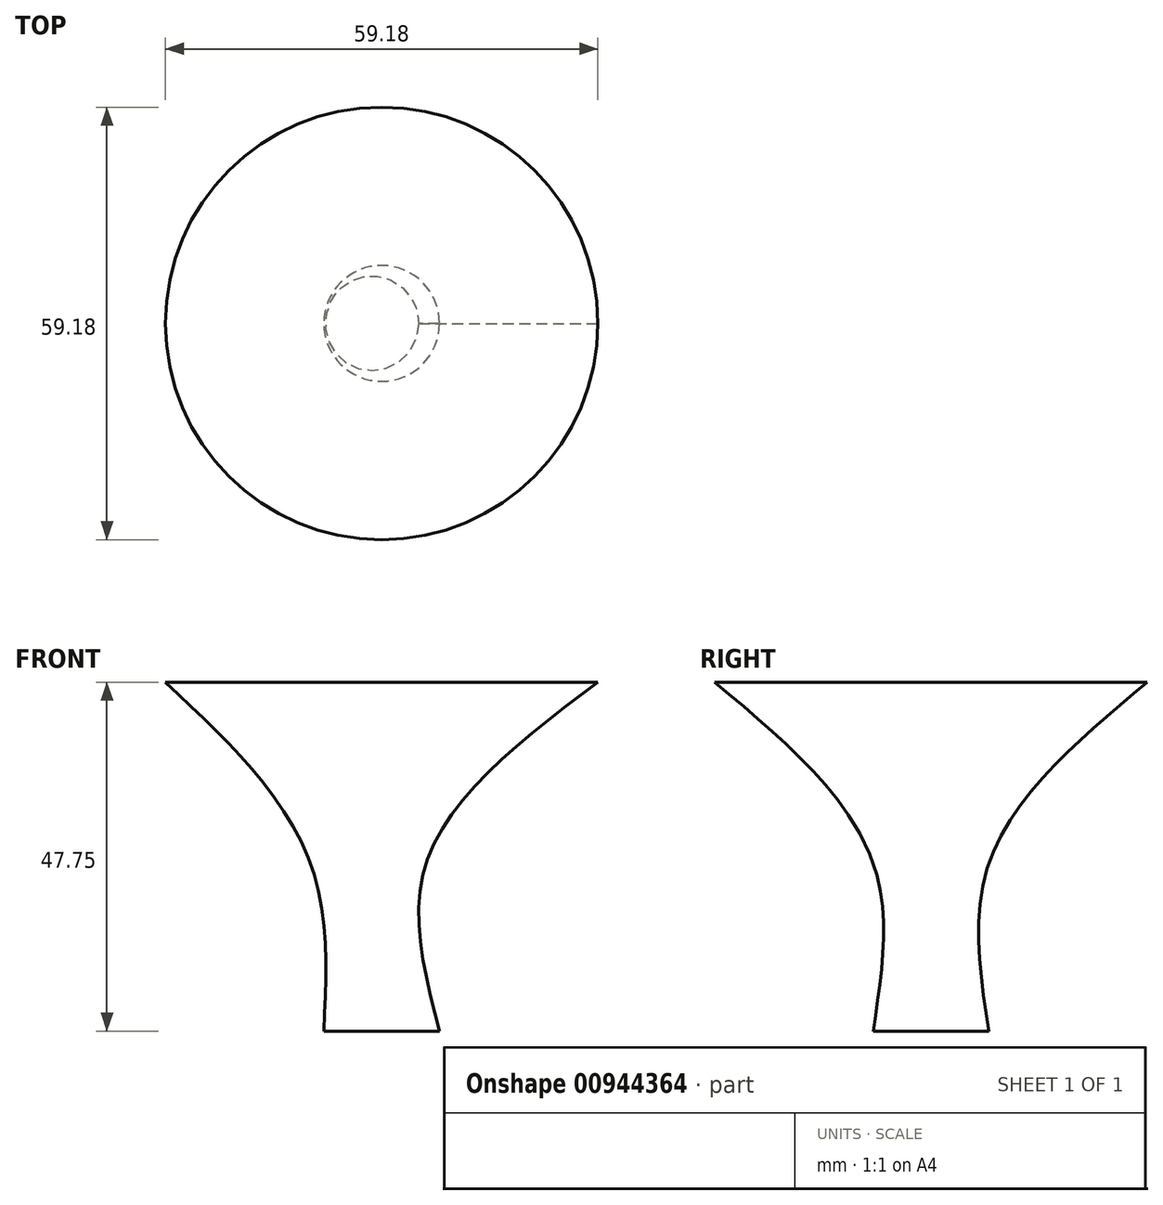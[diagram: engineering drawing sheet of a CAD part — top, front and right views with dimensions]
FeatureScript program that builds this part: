
annotation { "Feature Type Name" : "Feature", "Feature Type Description" : "" }
export const myFeature = defineFeature(function(context is Context, id is Id, definition is map)
    precondition{}
    {
        {
            var Q0;
            Q0=qCreatedBy(makeId("Top.planeOp"),FACE);
            cPlane(context, id + "F0", {"entities" : qUnion([Q0]), "cplaneType" : CPlaneType.OFFSET, "offset" : 47.75 * mm, "width" : 152.4 * mm, "height" : 152.4 * mm});
        }
        {
            var Q0;
            Q0=qCreatedBy(makeId("Top.planeOp"),FACE);
            var sketch = newSketch(context, id + "F1", { "sketchPlane" : qUnion([Q0])});
            skCircle(sketch, "E0", {"center": v(0, 0) * mm, "radius": 7.92 * mm});
            skSolve(sketch);
        }
        {
            var Q0;
            Q0=qCreatedBy(id+"F0.planeOp",FACE);
            var sketch = newSketch(context, id + "F2", { "sketchPlane" : qUnion([Q0])});
            skCircle(sketch, "E1", {"center": v(0, 0) * mm, "radius": 29.6 * mm});
            skSolve(sketch);
        }
        {
            var Q0;
            Q0=qCreatedBy(makeId("Top.planeOp"),FACE);
            cPlane(context, id + "F3", {"entities" : qUnion([Q0]), "cplaneType" : CPlaneType.OFFSET, "offset" : 21.08 * mm, "width" : 152.4 * mm, "height" : 152.4 * mm});
        }
        {
            var Q0;
            Q0=qCreatedBy(id+"F3.planeOp",FACE);
            var sketch = newSketch(context, id + "F4", { "sketchPlane" : qUnion([Q0])});
            skCircle(sketch, "E2", {"center": v(-1.77, 0) * mm, "radius": 7.35 * mm});
            skSolve(sketch);
        }
        {
            var Q0;
            Q0=makeQuery(id+"F1.imprint","IMPRINT",FACE,{"disambiguationData":[TD([[makeQuery(id+"F1.imprint","IMPRINT",EDGE,{"derivedFrom":sQuery(id+"F1.wireOp",EDGE,"E0")}),1.0]])]});
            var Q1;
            Q1=makeQuery(id+"F4.imprint","IMPRINT",FACE,{"disambiguationData":[TD([[makeQuery(id+"F4.imprint","IMPRINT",EDGE,{"derivedFrom":sQuery(id+"F4.wireOp",EDGE,"E2")}),1.0]])]});
            var Q2;
            Q2=makeQuery(id+"F2.imprint","IMPRINT",FACE,{"disambiguationData":[TD([[makeQuery(id+"F2.imprint","IMPRINT",EDGE,{"derivedFrom":sQuery(id+"F2.wireOp",EDGE,"E1")}),1.0]])]});
            loft(context, id + "F5", {"sheetProfilesArray" : [{ "sheetProfileEntities" : qUnion([Q0]) }, { "sheetProfileEntities" : qUnion([Q1]) }, { "sheetProfileEntities" : qUnion([Q2]) }]});
        }
    });
